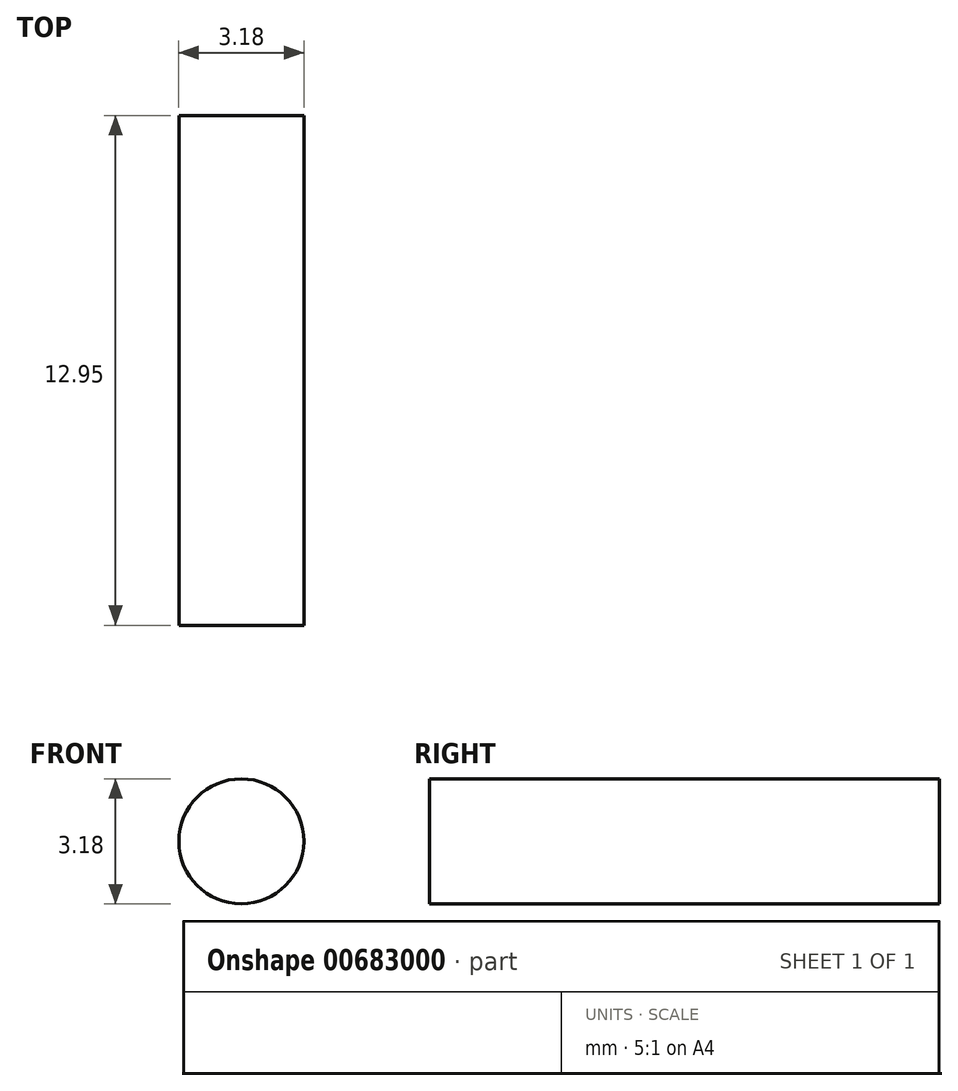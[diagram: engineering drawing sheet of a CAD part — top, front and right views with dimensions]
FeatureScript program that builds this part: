
annotation { "Feature Type Name" : "Feature", "Feature Type Description" : "" }
export const myFeature = defineFeature(function(context is Context, id is Id, definition is map)
    precondition{}
    {
        {
            var Q0;
            Q0=qCreatedBy(makeId("Front.planeOp"),FACE);
            var sketch = newSketch(context, id + "F0", { "sketchPlane" : qUnion([Q0])});
            skCircle(sketch, "E0", {"center": v(-44.8, 14.86) * mm, "radius": 1.59 * mm});
            skSolve(sketch);
        }
        {
            var Q0;
            Q0 = qSketchRegion(id + "F0", true);
            extrude(context, id + "F1", {"entities" : qUnion([Q0]), "depth" : 12.95 * mm, "offsetDistance" : 25.4 * mm});
        }
    });
